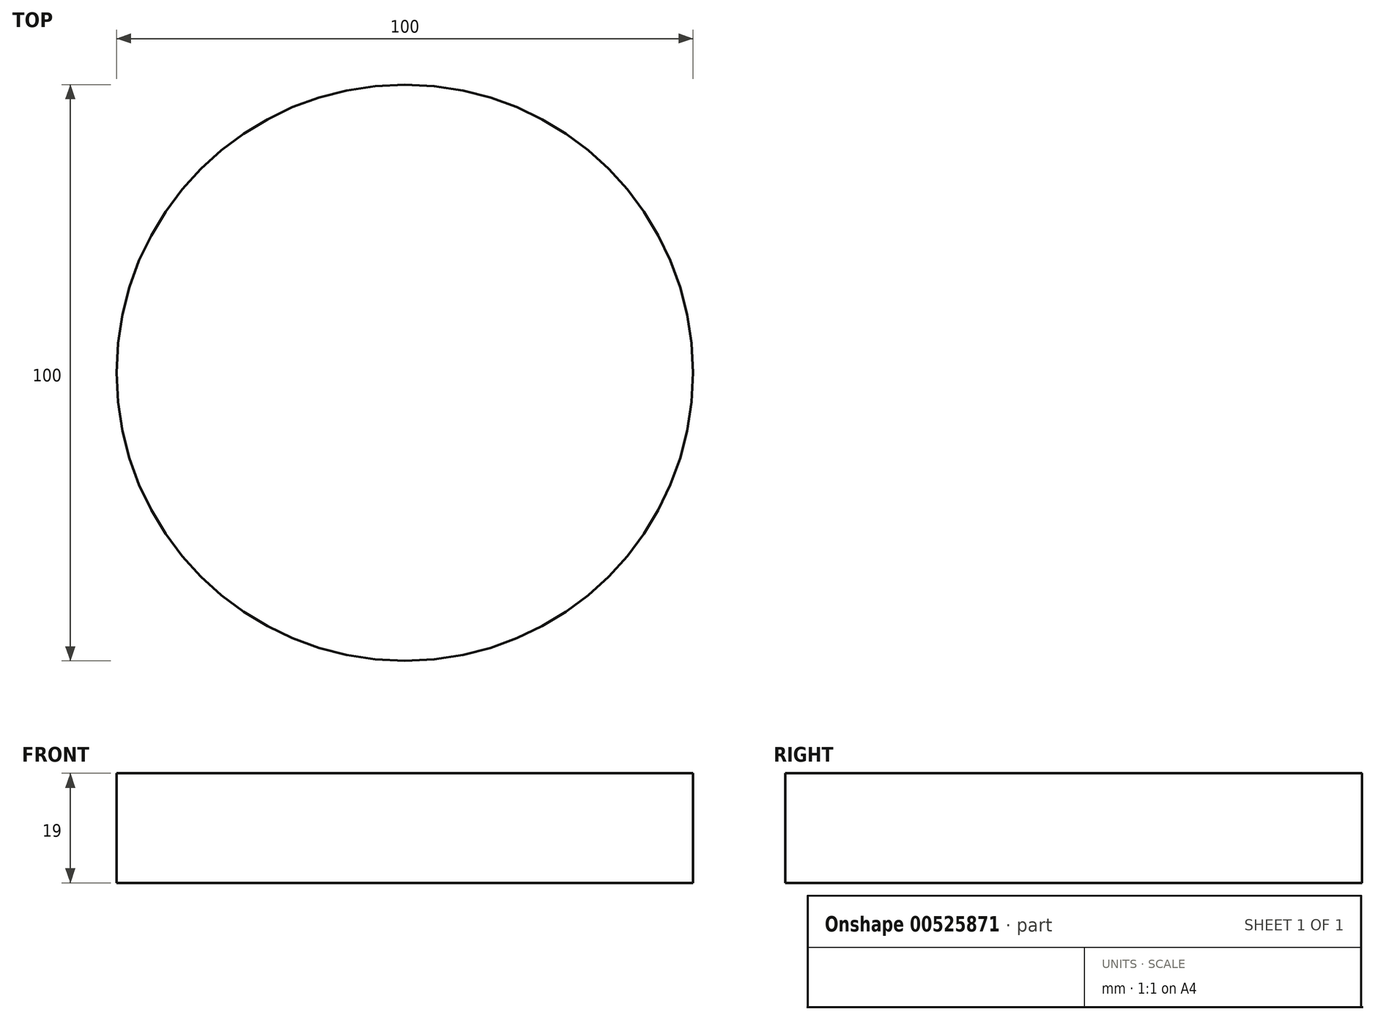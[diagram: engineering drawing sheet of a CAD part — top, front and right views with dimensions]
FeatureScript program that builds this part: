
annotation { "Feature Type Name" : "Feature", "Feature Type Description" : "" }
export const myFeature = defineFeature(function(context is Context, id is Id, definition is map)
    precondition{}
    {
        {
            var Q0;
            Q0=qCreatedBy(makeId("Top.planeOp"),FACE);
            var sketch = newSketch(context, id + "F0", { "sketchPlane" : qUnion([Q0])});
            skCircle(sketch, "E0", {"center": v(-19.26, 11.79) * mm, "radius": 50 * mm});
            skSolve(sketch);
        }
        {
            var Q0;
            Q0 = qSketchRegion(id + "F0", true);
            extrude(context, id + "F1", {"entities" : qUnion([Q0]), "depth" : 19 * mm, "offsetDistance" : 25 * mm});
        }
    });
